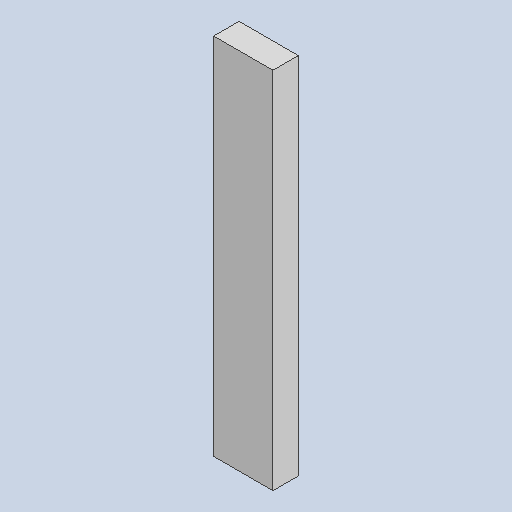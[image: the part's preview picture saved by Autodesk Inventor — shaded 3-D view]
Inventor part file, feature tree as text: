
AUTODESK INVENTOR PART (.ipt)
format: ipt  version: 2025 (Build 290162000, 162)  size: 79,360 bytes
history: native  units: in
note: dims shown in document units (in); Inventor stores cm internally (conversion verified against a paired STEP export)
features: other x3, sketch x1
ambient origin geometry x8: Origin, YZ Plane, XZ Plane, XY Plane, X Axis, Y Axis, Z Axis, Center Point
bodies: Solid1 (feature_tree)
feature tree (4):
  other  "side-slant_MIR.ipt"
  other  "Solid1::side-slant_MIR.ipt"
  other  "TaggingFeature1"
  sketch  "Sketch1"  dims[d0=0.3937in]
